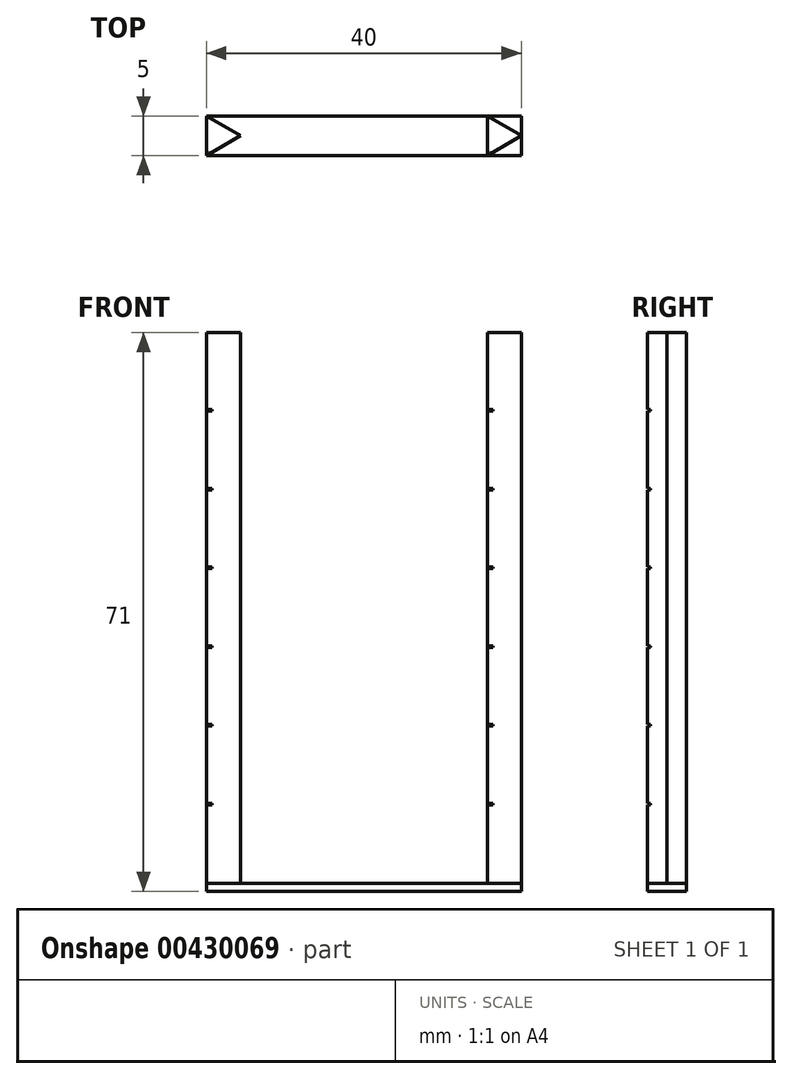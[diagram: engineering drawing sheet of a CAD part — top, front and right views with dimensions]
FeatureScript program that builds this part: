
annotation { "Feature Type Name" : "Feature", "Feature Type Description" : "" }
export const myFeature = defineFeature(function(context is Context, id is Id, definition is map)
    precondition{}
    {
        {
            var Q0;
            Q0=qCreatedBy(makeId("Top.planeOp"),FACE);
            var sketch = newSketch(context, id + "F0", { "sketchPlane" : qUnion([Q0])});
            skLineSegment(sketch, "E0.bottom", {"start": v(20, -2.5) * mm, "end": v(-20, -2.5) * mm});
            skLineSegment(sketch, "E0.top", {"start": v(20, 2.5) * mm, "end": v(-20, 2.5) * mm});
            skLineSegment(sketch, "E0.left", {"start": v(20, -2.5) * mm, "end": v(20, 2.5) * mm});
            skLineSegment(sketch, "E0.right", {"start": v(-20, -2.5) * mm, "end": v(-20, 2.5) * mm});
            skPoint(sketch, "E0.middle", {"position": v(0, 0) * mm});
            skSolve(sketch);
        }
        {
            var Q0;
            Q0 = qSketchRegion(id + "F0", true);
            extrude(context, id + "F1", {"entities" : qUnion([Q0]), "depth" : 1 * mm});
        }
        {
            var Q0;
            Q0=qCreatedBy(makeId("Top.planeOp"),FACE);
            var sketch = newSketch(context, id + "F2", { "sketchPlane" : qUnion([Q0])});
            skLineSegment(sketch, "E1", {"start": v(-20, 2.5) * mm, "end": v(-20, -2.5) * mm});
            skLineSegment(sketch, "E2", {"start": v(-20, -2.5) * mm, "end": v(-15.67, 0) * mm});
            skLineSegment(sketch, "E3", {"start": v(-15.67, 0) * mm, "end": v(-20, 2.5) * mm});
            skLineSegment(sketch, "E4", {"start": v(15.67, 2.5) * mm, "end": v(15.67, -2.5) * mm});
            skLineSegment(sketch, "E5", {"start": v(15.67, -2.5) * mm, "end": v(20, 0) * mm});
            skLineSegment(sketch, "E6", {"start": v(20, 0) * mm, "end": v(15.67, 2.5) * mm});
            skSolve(sketch);
        }
        {
            var Q0;
            Q0 = qSketchRegion(id + "F2", true);
            extrude(context, id + "F3", {"entities" : qUnion([Q0]), "operationType" : NewBodyOperationType.ADD, "depth" : 71 * mm});
        }
        {
            var Q0;
            Q0=makeQuery(id+"F3.boolean.opBoolean","MERGE",FACE,{"derivedFrom":[makeQuery(id+"F1.opExtrude","SWEPT_FACE",FACE,{"disambiguationData":[OSD([sQuery(id+"F0.wireOp",EDGE,"E0.right")])]}),makeQuery(id+"F3.opExtrude","SWEPT_FACE",FACE,{"disambiguationData":[OSD([sQuery(id+"F2.wireOp",EDGE,"E1")])]})]});
            var sketch = newSketch(context, id + "F4", { "sketchPlane" : qUnion([Q0])});
            skLineSegment(sketch, "E7.bottom", {"start": v(2.1, 11) * mm, "end": v(2.5, 11) * mm});
            skLineSegment(sketch, "E7.top", {"start": v(2.1, 11.2) * mm, "end": v(2.5, 11.2) * mm});
            skLineSegment(sketch, "E7.left", {"start": v(2.5, 11) * mm, "end": v(2.5, 11.2) * mm});
            skLineSegment(sketch, "E7.right", {"start": v(2.1, 11) * mm, "end": v(2.1, 11.2) * mm});
            skLineSegment(sketch, "E8.0.1.0", {"start": v(2.1, 21.2) * mm, "end": v(2.5, 21.2) * mm});
            skLineSegment(sketch, "E8.0.1.1", {"start": v(2.1, 21) * mm, "end": v(2.5, 21) * mm});
            skLineSegment(sketch, "E8.0.1.2", {"start": v(2.5, 21) * mm, "end": v(2.5, 21.2) * mm});
            skLineSegment(sketch, "E8.0.1.3", {"start": v(2.1, 21) * mm, "end": v(2.1, 21.2) * mm});
            skLineSegment(sketch, "E8.0.2.0", {"start": v(2.1, 31.2) * mm, "end": v(2.5, 31.2) * mm});
            skLineSegment(sketch, "E8.0.2.1", {"start": v(2.1, 31) * mm, "end": v(2.5, 31) * mm});
            skLineSegment(sketch, "E8.0.2.2", {"start": v(2.5, 31) * mm, "end": v(2.5, 31.2) * mm});
            skLineSegment(sketch, "E8.0.2.3", {"start": v(2.1, 31) * mm, "end": v(2.1, 31.2) * mm});
            skLineSegment(sketch, "E8.0.3.0", {"start": v(2.1, 41.2) * mm, "end": v(2.5, 41.2) * mm});
            skLineSegment(sketch, "E8.0.3.1", {"start": v(2.1, 41) * mm, "end": v(2.5, 41) * mm});
            skLineSegment(sketch, "E8.0.3.2", {"start": v(2.5, 41) * mm, "end": v(2.5, 41.2) * mm});
            skLineSegment(sketch, "E8.0.3.3", {"start": v(2.1, 41) * mm, "end": v(2.1, 41.2) * mm});
            skLineSegment(sketch, "E8.0.4.0", {"start": v(2.1, 51.2) * mm, "end": v(2.5, 51.2) * mm});
            skLineSegment(sketch, "E8.0.4.1", {"start": v(2.1, 51) * mm, "end": v(2.5, 51) * mm});
            skLineSegment(sketch, "E8.0.4.2", {"start": v(2.5, 51) * mm, "end": v(2.5, 51.2) * mm});
            skLineSegment(sketch, "E8.0.4.3", {"start": v(2.1, 51) * mm, "end": v(2.1, 51.2) * mm});
            skLineSegment(sketch, "E8.direction1", {"start": v(2.5, 11) * mm, "end": v(35.36, 11) * mm, "construction": true});
            skLineSegment(sketch, "E8.direction2", {"start": v(2.5, 11) * mm, "end": v(2.5, 21) * mm, "construction": true});
            skLineSegment(sketch, "E9.0.0.5", {"start": v(2.1, 61.2) * mm, "end": v(2.5, 61.2) * mm});
            skLineSegment(sketch, "E9.3.0.5", {"start": v(2.1, 61) * mm, "end": v(2.5, 61) * mm});
            skLineSegment(sketch, "E9.6.0.5", {"start": v(2.5, 61) * mm, "end": v(2.5, 61.2) * mm});
            skLineSegment(sketch, "E9.9.0.5", {"start": v(2.1, 61) * mm, "end": v(2.1, 61.2) * mm});
            skLineSegment(sketch, "E9.0.0.6", {"start": v(2.1, 71.2) * mm, "end": v(2.5, 71.2) * mm});
            skLineSegment(sketch, "E9.3.0.6", {"start": v(2.1, 71) * mm, "end": v(2.5, 71) * mm});
            skLineSegment(sketch, "E9.6.0.6", {"start": v(2.5, 71) * mm, "end": v(2.5, 71.2) * mm});
            skLineSegment(sketch, "E9.9.0.6", {"start": v(2.1, 71) * mm, "end": v(2.1, 71.2) * mm});
            skSolve(sketch);
        }
        {
            var Q0;
            Q0 = qSketchRegion(id + "F4", true);
            extrude(context, id + "F5", {"entities" : qUnion([Q0]), "operationType" : NewBodyOperationType.REMOVE, "endBound" : BoundingType.THROUGH_ALL, "oppositeDirection" : true, "depth" : 25 * mm});
        }
    });
